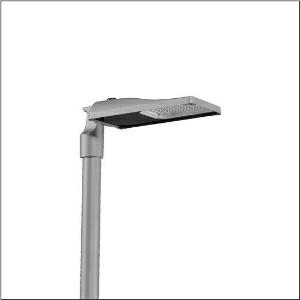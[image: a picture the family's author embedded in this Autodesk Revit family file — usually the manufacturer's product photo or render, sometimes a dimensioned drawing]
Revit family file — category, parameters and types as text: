
# Revit family: streetlight_sl_31_mini___st1_0a_5xh6d31s08ja_925e
name_source: partatom
category: Lighting Fixtures
units: mm (PartAtom-declared; Revit-internal decimal feet)

## family parameters
Cut with Voids When Loaded = No
Host = Face
Light Source = No
Part Type = Normal
Room Calculation Point = No
Round Connector Dimension = Use Diameter
Shared = No

## types (1)
- --- (1 x LED, 12270 lm, 82.5 W, 3000K)
    Apparent Load = 83 VA
    CIE Flux Codes = 40 73 97 100 100
    Color Rendering = 70
    Color Temperature = 3000K
    Default Elevation = 1800 mm
    Description = Streetlight SL 31 mini D4i, Desk-Remote mast luminaire for post-top, side-entry; light control with lens of PMMA; light distribution: ST1.0a, direct asymmetric distribution, for standard-compliant lighting for roads and squares; LED: luminous flux: 12.270lm, light colour: 730, colour temperature: 3000K; luminous efficacy: 148,7lm/W; control: pre-setting: logarithmic dimming characteristic, flexible luminous flux parameterisation, time-dependent luminous flux control, constant luminous flux control, power reduction, intelligent temperature release in ECG and LED module, overheat protection; luminaire housing, of diecast aluminium, SITECO metallic grey (DB 702S), corrosivity category C5 high according to DIN EN ISO 12944; cover of toughened safety glass, transparent, opened without tools; mast flange of diecast aluminium, SITECO metallic grey (DB 702S), spigot size: 76/60mm, mast flange included unmounted; with cable H07RN-F 2x 1.5mm², cable length: 10,5m, connection cable pre-assembled; mains connection: 220..240V, AC, 50/60Hz; power consumption (at start of service life): 82,5W / (at end of service life): 90,1W / (with reduced operation 50%): 36,8W; protection rating (complete): IP66; insulation class (complete): insulation class II (safety insulation); impact resistance: IK10; certification: CE, ENEC, ENEC+, VDE, UKCA, ZD4i; permissible operating ambient temperature for outdoor applications: -40..+50°C; packaging unit: 1 piece

Light Distribution: ST1.0a
    Height = 76 mm
    Lamp = 1 x LED
    Lamp Light Flux = 12270 lm
    Lamp Power = 82.5 W
    Lamp count = 1
    Length = 547 mm
    Luminous efficacy = 149 lm/W
    Manufacturer = Siteco
    ModVariant = No
    Model = 5XH6D31S08JA
    Number of Poles = 1
    OnlyDefault = Yes
    Power Factor = 1
    Product Name = Streetlight SL 31 mini | ST1.0a
    Product group = mast luminaire | pylon top
    ProductGroupID = 6100
    Protection Class = Protection class II
    Protection Degree = IP 66
    RLX_Detail_Level = 1
    RLX_Emergency_Light_Flux = 0 lm
    RLX_Emergency_Type = 0
    RLX_Emergency_Type_DB = No
    RlxData = <blob elided: 39789 chars, md5=6bb7c392>
    Socket = socket
    Standby Power = 0 W
    System Light Flux = 12270 lm
    System Power = 83 W
    Type Comments = factory setting: luminous flux: 100 % | dim-lin: 254 | 870 mA
    Type Image = l_1300330.jpg
    URL = http://relux.com
    VarID = @adj_057155
    Voltage = 0 V
    Weight = 0.00 kg
    Width = 265 mm

## geometry (parser evidence)
native form markers: Blend x4, Sweep x8
no freeform markers — native parametric forms only
